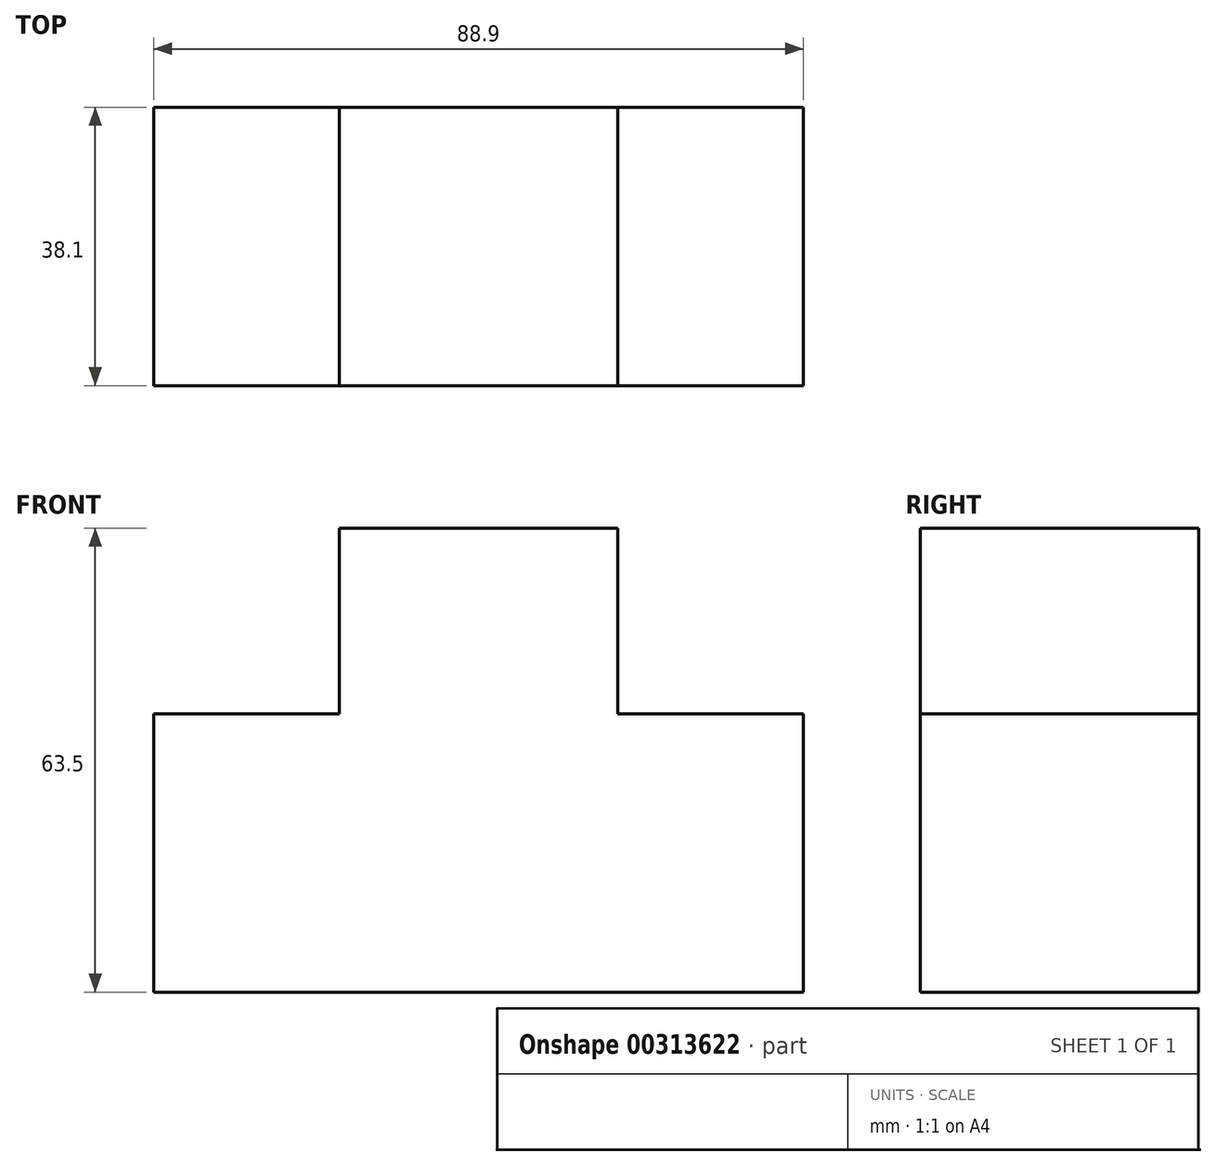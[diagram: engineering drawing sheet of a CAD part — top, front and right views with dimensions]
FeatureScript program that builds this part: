
annotation { "Feature Type Name" : "Feature", "Feature Type Description" : "" }
export const myFeature = defineFeature(function(context is Context, id is Id, definition is map)
    precondition{}
    {
        {
            var Q0;
            Q0=qCreatedBy(makeId("Front.planeOp"),FACE);
            var sketch = newSketch(context, id + "F0", { "sketchPlane" : qUnion([Q0])});
            skLineSegment(sketch, "E0", {"start": v(-42.77, -54.2) * mm, "end": v(46.13, -54.2) * mm});
            skLineSegment(sketch, "E1", {"start": v(-42.77, -54.2) * mm, "end": v(-42.77, -16.1) * mm});
            skLineSegment(sketch, "E2", {"start": v(46.13, -54.2) * mm, "end": v(46.13, -16.1) * mm});
            skLineSegment(sketch, "E3", {"start": v(46.13, -16.1) * mm, "end": v(20.73, -16.1) * mm});
            skLineSegment(sketch, "E4", {"start": v(-17.37, -16.1) * mm, "end": v(-17.37, 9.3) * mm});
            skLineSegment(sketch, "E5", {"start": v(20.73, 9.3) * mm, "end": v(20.73, -16.1) * mm});
            skLineSegment(sketch, "E6", {"start": v(-17.37, 9.3) * mm, "end": v(20.73, 9.3) * mm});
            skLineSegment(sketch, "E7", {"start": v(-17.37, -16.1) * mm, "end": v(-42.77, -16.1) * mm});
            skSolve(sketch);
        }
        {
            var Q0;
            Q0=makeQuery(id+"F0.imprint","IMPRINT",FACE,{"disambiguationData":[TD([[makeQuery(id+"F0.imprint","IMPRINT",EDGE,{"derivedFrom":sQuery(id+"F0.wireOp",EDGE,"E0")}),1.0]])]});
            extrude(context, id + "F1", {"entities" : qUnion([Q0]), "depth" : 38.1 * mm});
        }
    });
